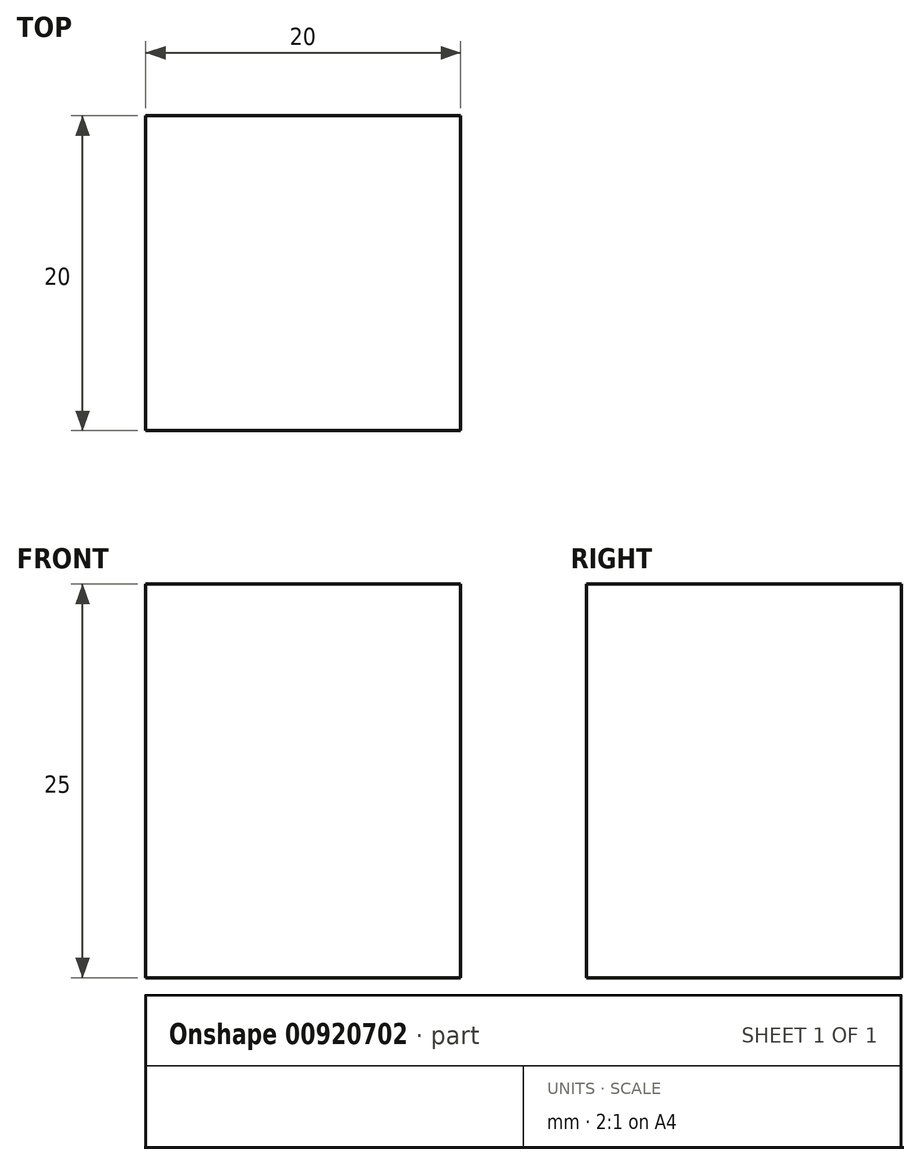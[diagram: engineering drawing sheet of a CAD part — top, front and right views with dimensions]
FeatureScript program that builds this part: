
annotation { "Feature Type Name" : "Feature", "Feature Type Description" : "" }
export const myFeature = defineFeature(function(context is Context, id is Id, definition is map)
    precondition{}
    {
        {
            var Q0;
            Q0=qCreatedBy(makeId("Top.planeOp"),FACE);
            var sketch = newSketch(context, id + "F0", { "sketchPlane" : qUnion([Q0])});
            skLineSegment(sketch, "E0.bottom", {"start": v(-10, 10) * mm, "end": v(10, 10) * mm});
            skLineSegment(sketch, "E0.top", {"start": v(-10, -10) * mm, "end": v(10, -10) * mm});
            skLineSegment(sketch, "E0.left", {"start": v(-10, 10) * mm, "end": v(-10, -10) * mm});
            skLineSegment(sketch, "E0.right", {"start": v(10, 10) * mm, "end": v(10, -10) * mm});
            skSolve(sketch);
        }
        {
            var Q0;
            Q0 = qSketchRegion(id + "F0", true);
            extrude(context, id + "F1", {"entities" : qUnion([Q0]), "depth" : 25 * mm, "offsetDistance" : 25 * mm});
        }
    });
